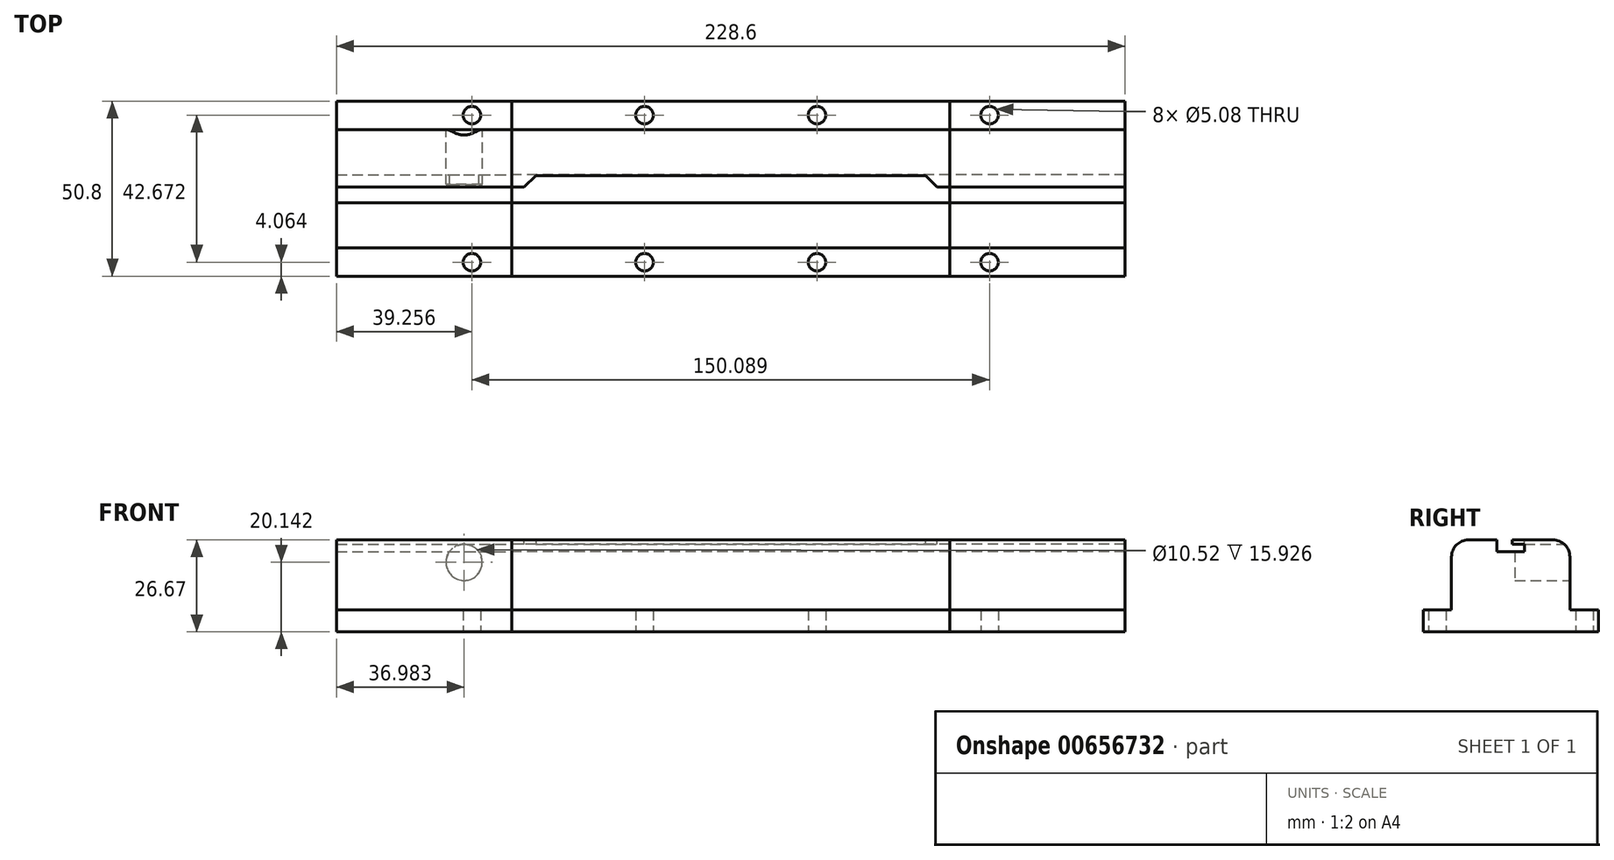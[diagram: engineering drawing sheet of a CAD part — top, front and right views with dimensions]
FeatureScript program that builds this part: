
annotation { "Feature Type Name" : "Feature", "Feature Type Description" : "" }
export const myFeature = defineFeature(function(context is Context, id is Id, definition is map)
    precondition{}
    {
        {
            var Q0;
            Q0=qCreatedBy(makeId("Top.planeOp"),FACE);
            var sketch = newSketch(context, id + "F0", { "sketchPlane" : qUnion([Q0])});
            skLineSegment(sketch, "E0.bottom", {"start": v(63.5, -25.4) * mm, "end": v(-63.5, -25.4) * mm});
            skLineSegment(sketch, "E0.top", {"start": v(63.5, 25.4) * mm, "end": v(-63.5, 25.4) * mm});
            skLineSegment(sketch, "E0.left", {"start": v(63.5, -25.4) * mm, "end": v(63.5, 25.4) * mm});
            skLineSegment(sketch, "E0.right", {"start": v(-63.5, -25.4) * mm, "end": v(-63.5, 25.4) * mm});
            skPoint(sketch, "E0.middle", {"position": v(0, 0) * mm});
            skSolve(sketch);
        }
        {
            var Q0;
            Q0=makeQuery(id+"F0.imprint","IMPRINT",FACE,{"disambiguationData":[TD([[makeQuery(id+"F0.imprint","IMPRINT",EDGE,{"derivedFrom":sQuery(id+"F0.wireOp",EDGE,"E0.bottom")}),-1.0]])]});
            extrude(context, id + "F1", {"entities" : qUnion([Q0]), "depth" : 25.4 * mm, "offsetDistance" : 25.4 * mm});
        }
        {
            var Q0;
            Q0=makeQuery(id+"F1.opExtrude","CAP_FACE",FACE,{"disambiguationData":[OSD([sQuery(id+"F0.wireOp",EDGE,"E0.bottom"),sQuery(id+"F0.wireOp",EDGE,"E0.top"),sQuery(id+"F0.wireOp",EDGE,"E0.left"),sQuery(id+"F0.wireOp",EDGE,"E0.right")])],"isStart":false});
            var sketch = newSketch(context, id + "F2", { "sketchPlane" : qUnion([Q0])});
            skLineSegment(sketch, "E1.bottom", {"start": v(63.5, -4.03) * mm, "end": v(-63.5, -4.03) * mm});
            skLineSegment(sketch, "E1.top", {"start": v(63.5, 4.03) * mm, "end": v(-63.5, 4.03) * mm});
            skLineSegment(sketch, "E1.left", {"start": v(63.5, -4.03) * mm, "end": v(63.5, 4.03) * mm});
            skLineSegment(sketch, "E1.right", {"start": v(-63.5, -4.03) * mm, "end": v(-63.5, 4.03) * mm});
            skPoint(sketch, "E1.middle", {"position": v(0, 0) * mm});
            skSolve(sketch);
        }
        {
            var Q0;
            Q0 = qSketchRegion(id + "F2", true);
            extrude(context, id + "F3", {"entities" : qUnion([Q0]), "operationType" : NewBodyOperationType.REMOVE, "oppositeDirection" : true, "depth" : 2.16 * mm, "offsetDistance" : 25.4 * mm});
        }
        {
            var Q0;
            {var subQ0=sQuery(id+"F0.wireOp",EDGE,"E0.bottom");var subQ1=sQuery(id+"F0.wireOp",EDGE,"E0.right");var subQ2=sQuery(id+"F0.wireOp",EDGE,"E0.left");Q0=makeQuery(id+"F3.boolean.opBoolean","SPLIT",FACE,{"disambiguationData":[TD([makeQuery(id+"F1.opExtrude","SWEPT_FACE",FACE,{"disambiguationData":[OSD([subQ0])]})])],"derivedFrom":makeQuery(id+"F1.opExtrude","CAP_FACE",FACE,{"disambiguationData":[OSD([subQ0,sQuery(id+"F0.wireOp",EDGE,"E0.top"),subQ2,subQ1])],"isStart":false})});}
            var sketch = newSketch(context, id + "F4", { "sketchPlane" : qUnion([Q0])});
            skLineSegment(sketch, "E2.bottom", {"start": v(-63.5, -25.4) * mm, "end": v(63.5, -25.4) * mm});
            skLineSegment(sketch, "E2.top", {"start": v(-63.5, -17.15) * mm, "end": v(63.5, -17.15) * mm});
            skLineSegment(sketch, "E2.left", {"start": v(-63.5, -25.4) * mm, "end": v(-63.5, -17.15) * mm});
            skLineSegment(sketch, "E2.right", {"start": v(63.5, -25.4) * mm, "end": v(63.5, -17.15) * mm});
            skLineSegment(sketch, "E3.bottom", {"start": v(-63.5, 25.4) * mm, "end": v(63.5, 25.4) * mm});
            skLineSegment(sketch, "E3.top", {"start": v(-63.5, 17.15) * mm, "end": v(63.5, 17.15) * mm});
            skLineSegment(sketch, "E3.left", {"start": v(-63.5, 25.4) * mm, "end": v(-63.5, 17.15) * mm});
            skLineSegment(sketch, "E3.right", {"start": v(63.5, 25.4) * mm, "end": v(63.5, 17.15) * mm});
            skSolve(sketch);
        }
        {
            var Q0;
            Q0 = qSketchRegion(id + "F4", true);
            extrude(context, id + "F5", {"entities" : qUnion([Q0]), "operationType" : NewBodyOperationType.REMOVE, "oppositeDirection" : true, "depth" : 19.05 * mm, "offsetDistance" : 25.4 * mm});
        }
        {
            var Q0;
            {var subQ0=sQuery(id+"F0.wireOp",EDGE,"E0.top");var subQ1=sQuery(id+"F0.wireOp",EDGE,"E0.left");var subQ2=sQuery(id+"F0.wireOp",EDGE,"E0.right");Q0=makeQuery(id+"F3.boolean.opBoolean","SPLIT",FACE,{"disambiguationData":[TD([makeQuery(id+"F1.opExtrude","SWEPT_FACE",FACE,{"disambiguationData":[OSD([subQ0])]})])],"derivedFrom":makeQuery(id+"F1.opExtrude","CAP_FACE",FACE,{"disambiguationData":[OSD([sQuery(id+"F0.wireOp",EDGE,"E0.bottom"),subQ0,subQ1,subQ2])],"isStart":false})});}
            var sketch = newSketch(context, id + "F6", { "sketchPlane" : qUnion([Q0])});
            skLineSegment(sketch, "E4.bottom", {"start": v(-63.5, 17.15) * mm, "end": v(63.5, 17.15) * mm});
            skLineSegment(sketch, "E4.top", {"start": v(-63.5, -17.15) * mm, "end": v(63.5, -17.15) * mm});
            skLineSegment(sketch, "E4.left", {"start": v(-63.5, 17.15) * mm, "end": v(-63.5, -17.15) * mm});
            skLineSegment(sketch, "E4.right", {"start": v(63.5, 17.15) * mm, "end": v(63.5, -17.15) * mm});
            skPoint(sketch, "E4.middle", {"position": v(0, 0) * mm});
            skSolve(sketch);
        }
        {
            var Q0;
            Q0 = qSketchRegion(id + "F6", true);
            extrude(context, id + "F7", {"entities" : qUnion([Q0]), "operationType" : NewBodyOperationType.ADD, "depth" : 1.27 * mm, "offsetDistance" : 25.4 * mm});
        }
        {
            var Q0;
            Q0=makeQuery(id+"F3.boolean.opBoolean","COPY",FACE,{"derivedFrom":makeQuery(id+"F3.opExtrude","CAP_FACE",FACE,{"disambiguationData":[OSD([sQuery(id+"F2.wireOp",EDGE,"E1.bottom"),sQuery(id+"F2.wireOp",EDGE,"E1.top"),sQuery(id+"F2.wireOp",EDGE,"E1.left"),sQuery(id+"F2.wireOp",EDGE,"E1.right")])],"isStart":false})});
            var sketch = newSketch(context, id + "F8", { "sketchPlane" : qUnion([Q0])});
            skLineSegment(sketch, "E5.bottom", {"start": v(-63.5, -4.03) * mm, "end": v(63.5, -4.03) * mm});
            skLineSegment(sketch, "E5.top", {"start": v(-63.5, 0.45) * mm, "end": v(63.5, 0.45) * mm});
            skLineSegment(sketch, "E5.left", {"start": v(-63.5, -4.03) * mm, "end": v(-63.5, 0.45) * mm});
            skLineSegment(sketch, "E5.right", {"start": v(63.5, -4.03) * mm, "end": v(63.5, 0.45) * mm});
            skSolve(sketch);
        }
        {
            var Q0;
            Q0 = qSketchRegion(id + "F8", true);
            extrude(context, id + "F9", {"entities" : qUnion([Q0]), "operationType" : NewBodyOperationType.REMOVE, "depth" : 5.33 * mm, "offsetDistance" : 25.4 * mm});
        }
        {
            var Q0;
            {var subQ0=sQuery(id+"F6.wireOp",EDGE,"E4.bottom");var subQ1=sQuery(id+"F6.wireOp",EDGE,"E4.left");var subQ2=sQuery(id+"F6.wireOp",EDGE,"E4.right");Q0=makeQuery(id+"F9.boolean.opBoolean","SPLIT",FACE,{"disambiguationData":[TD([makeQuery(id+"F5.boolean.opBoolean","COPY",FACE,{"derivedFrom":makeQuery(id+"F5.opExtrude","SWEPT_FACE",FACE,{"disambiguationData":[OSD([sQuery(id+"F4.wireOp",EDGE,"E3.top")])]})})])],"derivedFrom":makeQuery(id+"F7.opExtrude","CAP_FACE",FACE,{"disambiguationData":[OSD([subQ0,sQuery(id+"F6.wireOp",EDGE,"E4.top"),subQ1,subQ2])],"isStart":false})});}
            var sketch = newSketch(context, id + "F10", { "sketchPlane" : qUnion([Q0])});
            skLineSegment(sketch, "E6.bottom", {"start": v(-60.33, 3.81) * mm, "end": v(60.33, 3.81) * mm});
            skLineSegment(sketch, "E6.top", {"start": v(-60.33, -3.81) * mm, "end": v(60.33, -3.81) * mm});
            skLineSegment(sketch, "E6.left", {"start": v(-60.33, 3.81) * mm, "end": v(-60.33, -3.81) * mm});
            skLineSegment(sketch, "E6.right", {"start": v(60.33, 3.8) * mm, "end": v(60.33, -3.81) * mm});
            skPoint(sketch, "E6.middle", {"position": v(0, 0) * mm});
            skSolve(sketch);
        }
        {
            var Q0;
            Q0 = qSketchRegion(id + "F10", true);
            extrude(context, id + "F11", {"entities" : qUnion([Q0]), "operationType" : NewBodyOperationType.REMOVE, "oppositeDirection" : true, "depth" : 1.52 * mm, "offsetDistance" : 25.4 * mm});
        }
        {
            var Q0;
            Q0=makeQuery(id+"F11.boolean.opBoolean","COPY",EDGE,{"derivedFrom":makeQuery(id+"F11.opExtrude","SWEPT_EDGE",EDGE,{"disambiguationData":[OSD([sQuery(id+"F10.wireOp",EDGE,"E6.bottom"),sQuery(id+"F10.wireOp",EDGE,"E6.right")])]})});
            var Q1;
            Q1=makeQuery(id+"F11.boolean.opBoolean","COPY",EDGE,{"derivedFrom":makeQuery(id+"F11.opExtrude","SWEPT_EDGE",EDGE,{"disambiguationData":[OSD([sQuery(id+"F10.wireOp",EDGE,"E6.bottom"),sQuery(id+"F10.wireOp",EDGE,"E6.left")])]})});
            chamfer(context, id + "F12", {"entities" : qUnion([Q0, Q1]), "width" : 3.8 * mm, "tangentPropagation" : true});
        }
        {
            var Q0;
            Q0=makeQuery(id+"F7.boolean.opBoolean","MERGE",FACE,{"derivedFrom":[makeQuery(id+"F1.opExtrude","SWEPT_FACE",FACE,{"disambiguationData":[OSD([sQuery(id+"F0.wireOp",EDGE,"E0.right")])]}),makeQuery(id+"F7.opExtrude","SWEPT_FACE",FACE,{"disambiguationData":[OSD([sQuery(id+"F6.wireOp",EDGE,"E4.left")])]})]});
            extrude(context, id + "F13", {"entities" : qUnion([Q0]), "depth" : 50.8 * mm, "offsetDistance" : 25.4 * mm});
        }
        {
            var Q0;
            Q0=makeQuery(id+"F7.boolean.opBoolean","MERGE",FACE,{"derivedFrom":[makeQuery(id+"F1.opExtrude","SWEPT_FACE",FACE,{"disambiguationData":[OSD([sQuery(id+"F0.wireOp",EDGE,"E0.left")])]}),makeQuery(id+"F7.opExtrude","SWEPT_FACE",FACE,{"disambiguationData":[OSD([sQuery(id+"F6.wireOp",EDGE,"E4.right")])]})]});
            extrude(context, id + "F14", {"entities" : qUnion([Q0]), "depth" : 50.8 * mm, "offsetDistance" : 25.4 * mm});
        }
        {
            var Q0;
            Q0=qCreatedBy(makeId("Top.planeOp"),FACE);
            var sketch = newSketch(context, id + "F15", { "sketchPlane" : qUnion([Q0])});
            skPoint(sketch, "E7.middle", {"position": v(0, 0) * mm});
            skCircle(sketch, "E8", {"center": v(-25, 21.34) * mm, "radius": 2.54 * mm});
            skCircle(sketch, "E9", {"center": v(25, 21.34) * mm, "radius": 2.54 * mm});
            skCircle(sketch, "E10", {"center": v(25, -21.34) * mm, "radius": 2.54 * mm});
            skCircle(sketch, "E11", {"center": v(-25, -21.34) * mm, "radius": 2.54 * mm});
            skCircle(sketch, "E12", {"center": v(-75.04, 21.34) * mm, "radius": 2.54 * mm});
            skCircle(sketch, "E13", {"center": v(-75.04, -21.34) * mm, "radius": 2.54 * mm});
            skCircle(sketch, "E14", {"center": v(75.04, 21.34) * mm, "radius": 2.54 * mm});
            skCircle(sketch, "E15", {"center": v(75.04, -21.34) * mm, "radius": 2.54 * mm});
            skSolve(sketch);
        }
        {
            var Q0;
            Q0 = qSketchRegion(id + "F15", true);
            extrude(context, id + "F16", {"entities" : qUnion([Q0]), "operationType" : NewBodyOperationType.REMOVE, "depth" : 47.24 * mm, "offsetDistance" : 25.4 * mm});
        }
        {
            var Q0;
            Q0=makeQuery(id+"F13.opExtrude","SWEPT_FACE",FACE,{"disambiguationData":[OSD([sQuery(id+"F4.wireOp",EDGE,"E3.top"),sQuery(id+"F4.wireOp",EDGE,"E3.left"),sQuery(id+"F6.wireOp",EDGE,"E4.bottom"),sQuery(id+"F6.wireOp",EDGE,"E4.left")])]});
            var sketch = newSketch(context, id + "F17", { "sketchPlane" : qUnion([Q0])});
            skCircle(sketch, "E16", {"center": v(77.32, 20.14) * mm, "radius": 5.26 * mm});
            skSolve(sketch);
        }
        {
            var Q0;
            Q0 = qSketchRegion(id + "F17", true);
            extrude(context, id + "F18", {"entities" : qUnion([Q0]), "operationType" : NewBodyOperationType.REMOVE, "oppositeDirection" : true, "depth" : 15.93 * mm, "offsetDistance" : 25.4 * mm});
        }
        {
            var Q0;
            Q0=makeQuery(id+"F13.opExtrude","SWEPT_EDGE",EDGE,{"disambiguationData":[OSD([sQuery(id+"F6.wireOp",EDGE,"E4.top"),sQuery(id+"F6.wireOp",EDGE,"E4.left")])]});
            var Q1;
            Q1=makeQuery(id+"F7.opExtrude","CAP_EDGE",EDGE,{"disambiguationData":[OSD([sQuery(id+"F6.wireOp",EDGE,"E4.top")])],"isStart":false});
            var Q2;
            Q2=makeQuery(id+"F14.opExtrude","SWEPT_EDGE",EDGE,{"disambiguationData":[OSD([sQuery(id+"F6.wireOp",EDGE,"E4.top"),sQuery(id+"F6.wireOp",EDGE,"E4.right")])]});
            var Q3;
            Q3=makeQuery(id+"F14.opExtrude","SWEPT_EDGE",EDGE,{"disambiguationData":[OSD([sQuery(id+"F6.wireOp",EDGE,"E4.bottom"),sQuery(id+"F6.wireOp",EDGE,"E4.right")])]});
            var Q4;
            Q4=makeQuery(id+"F7.opExtrude","CAP_EDGE",EDGE,{"disambiguationData":[OSD([sQuery(id+"F6.wireOp",EDGE,"E4.bottom")])],"isStart":false});
            var Q5;
            Q5=makeQuery(id+"F13.opExtrude","SWEPT_EDGE",EDGE,{"disambiguationData":[OSD([sQuery(id+"F6.wireOp",EDGE,"E4.bottom"),sQuery(id+"F6.wireOp",EDGE,"E4.left")])]});
            fillet(context, id + "F19", {"entities" : qUnion([Q0, Q1, Q2, Q3, Q4, Q5]), "radius" : 4.9 * mm, "tangentPropagation" : true, "allowEdgeOverflow" : false});
        }
    });
